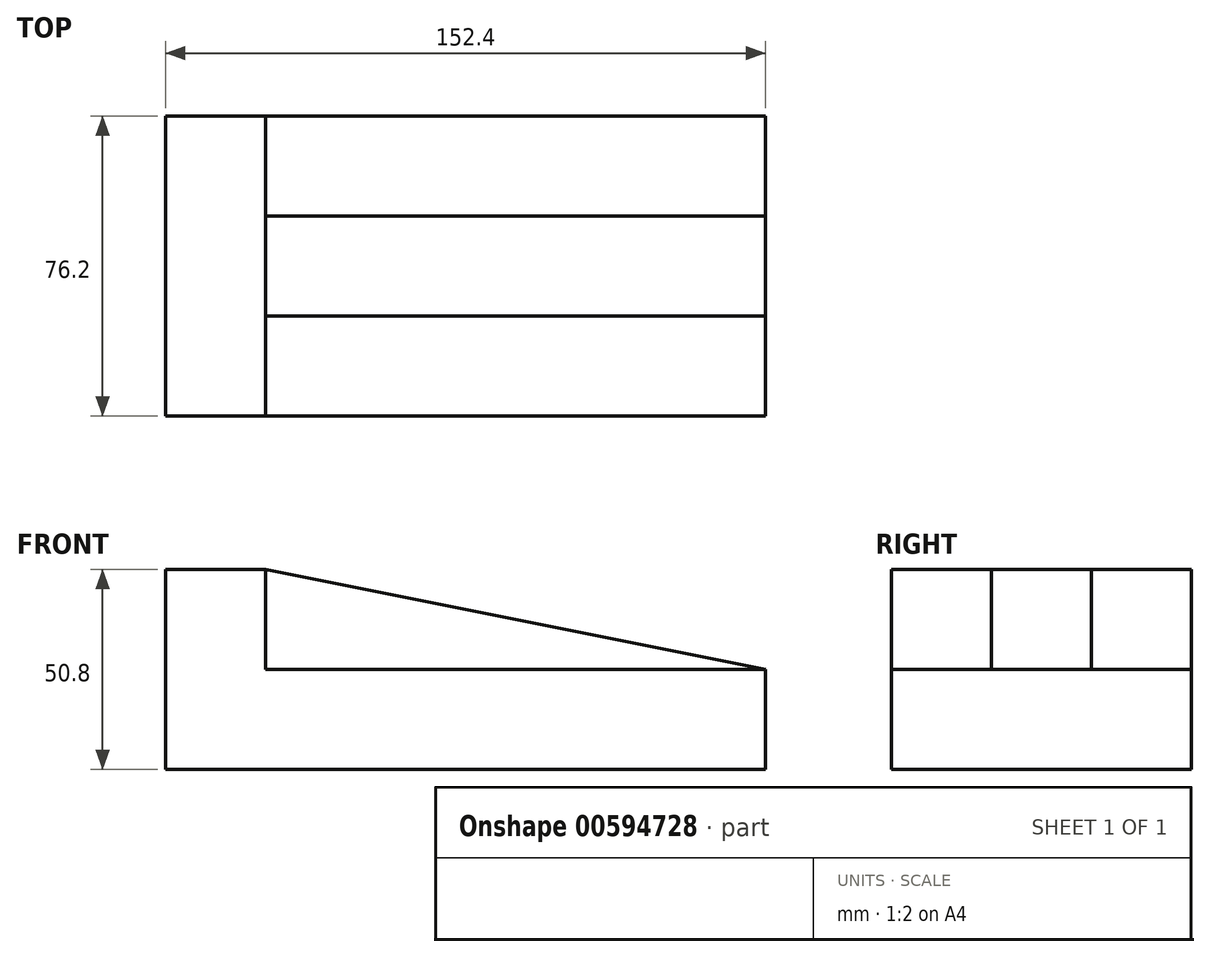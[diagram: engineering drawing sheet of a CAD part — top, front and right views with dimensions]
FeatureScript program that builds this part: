
annotation { "Feature Type Name" : "Feature", "Feature Type Description" : "" }
export const myFeature = defineFeature(function(context is Context, id is Id, definition is map)
    precondition{}
    {
        {
            var Q0;
            Q0=qCreatedBy(makeId("Front.planeOp"),FACE);
            var sketch = newSketch(context, id + "F0", { "sketchPlane" : qUnion([Q0])});
            skLineSegment(sketch, "E0.bottom", {"start": v(0, 0) * mm, "end": v(152.4, 0) * mm});
            skLineSegment(sketch, "E0.top", {"start": v(0, 50.8) * mm, "end": v(152.4, 50.8) * mm});
            skLineSegment(sketch, "E0.left", {"start": v(0, 0) * mm, "end": v(0, 50.8) * mm});
            skLineSegment(sketch, "E0.right", {"start": v(152.4, 0) * mm, "end": v(152.4, 50.8) * mm});
            skSolve(sketch);
        }
        {
            var Q0;
            Q0=makeQuery(id+"F0.imprint","IMPRINT",FACE,{"disambiguationData":[TD([[makeQuery(id+"F0.imprint","IMPRINT",EDGE,{"derivedFrom":sQuery(id+"F0.wireOp",EDGE,"E0.bottom")}),1.0]])]});
            extrude(context, id + "F1", {"entities" : qUnion([Q0]), "oppositeDirection" : true, "depth" : 76.2 * mm, "offsetDistance" : 25.4 * mm});
        }
        {
            var Q0;
            Q0=makeQuery(id+"F1.opExtrude","SWEPT_FACE",FACE,{"disambiguationData":[OSD([sQuery(id+"F0.wireOp",EDGE,"E0.right")])]});
            var sketch = newSketch(context, id + "F2", { "sketchPlane" : qUnion([Q0])});
            skLineSegment(sketch, "E1.bottom", {"start": v(0, 50.8) * mm, "end": v(25.4, 50.8) * mm});
            skLineSegment(sketch, "E1.top", {"start": v(0, 25.4) * mm, "end": v(25.4, 25.4) * mm});
            skLineSegment(sketch, "E1.left", {"start": v(0, 50.8) * mm, "end": v(0, 25.4) * mm});
            skLineSegment(sketch, "E1.right", {"start": v(25.4, 50.8) * mm, "end": v(25.4, 25.4) * mm});
            skLineSegment(sketch, "E2.bottom", {"start": v(76.2, 50.8) * mm, "end": v(50.8, 50.8) * mm});
            skLineSegment(sketch, "E2.top", {"start": v(76.2, 25.4) * mm, "end": v(50.8, 25.4) * mm});
            skLineSegment(sketch, "E2.left", {"start": v(76.2, 50.8) * mm, "end": v(76.2, 25.4) * mm});
            skLineSegment(sketch, "E2.right", {"start": v(50.8, 50.8) * mm, "end": v(50.8, 25.4) * mm});
            skSolve(sketch);
        }
        {
            var Q0;
            Q0=makeQuery(id+"F2.imprint","IMPRINT",FACE,{"disambiguationData":[TD([[makeQuery(id+"F2.imprint","IMPRINT",EDGE,{"derivedFrom":sQuery(id+"F2.wireOp",EDGE,"E1.bottom")}),1.0]])]});
            extrude(context, id + "F3", {"entities" : qUnion([Q0]), "operationType" : NewBodyOperationType.REMOVE, "oppositeDirection" : true, "depth" : 127 * mm, "offsetDistance" : 25.4 * mm});
        }
        {
            var Q0;
            Q0 = qSketchRegion(id + "F2", true);
            extrude(context, id + "F4", {"entities" : qUnion([Q0]), "operationType" : NewBodyOperationType.REMOVE, "oppositeDirection" : true, "depth" : 127 * mm, "offsetDistance" : 25.4 * mm});
        }
        {
            var Q0;
            Q0=makeQuery(id+"F3.boolean.opBoolean","COPY",FACE,{"derivedFrom":makeQuery(id+"F3.opExtrude","SWEPT_FACE",FACE,{"disambiguationData":[OSD([sQuery(id+"F2.wireOp",EDGE,"E1.right")])]})});
            var sketch = newSketch(context, id + "F5", { "sketchPlane" : qUnion([Q0])});
            skLineSegment(sketch, "E3", {"start": v(152.4, 50.8) * mm, "end": v(25.4, 50.8) * mm});
            skLineSegment(sketch, "E4", {"start": v(25.4, 50.8) * mm, "end": v(152.4, 25.4) * mm});
            skLineSegment(sketch, "E5", {"start": v(152.4, 25.4) * mm, "end": v(152.4, 50.8) * mm});
            skSolve(sketch);
        }
        {
            var Q0;
            Q0 = qSketchRegion(id + "F5", true);
            extrude(context, id + "F6", {"entities" : qUnion([Q0]), "operationType" : NewBodyOperationType.REMOVE, "oppositeDirection" : true, "depth" : 55.12 * mm, "offsetDistance" : 25.4 * mm});
        }
    });
